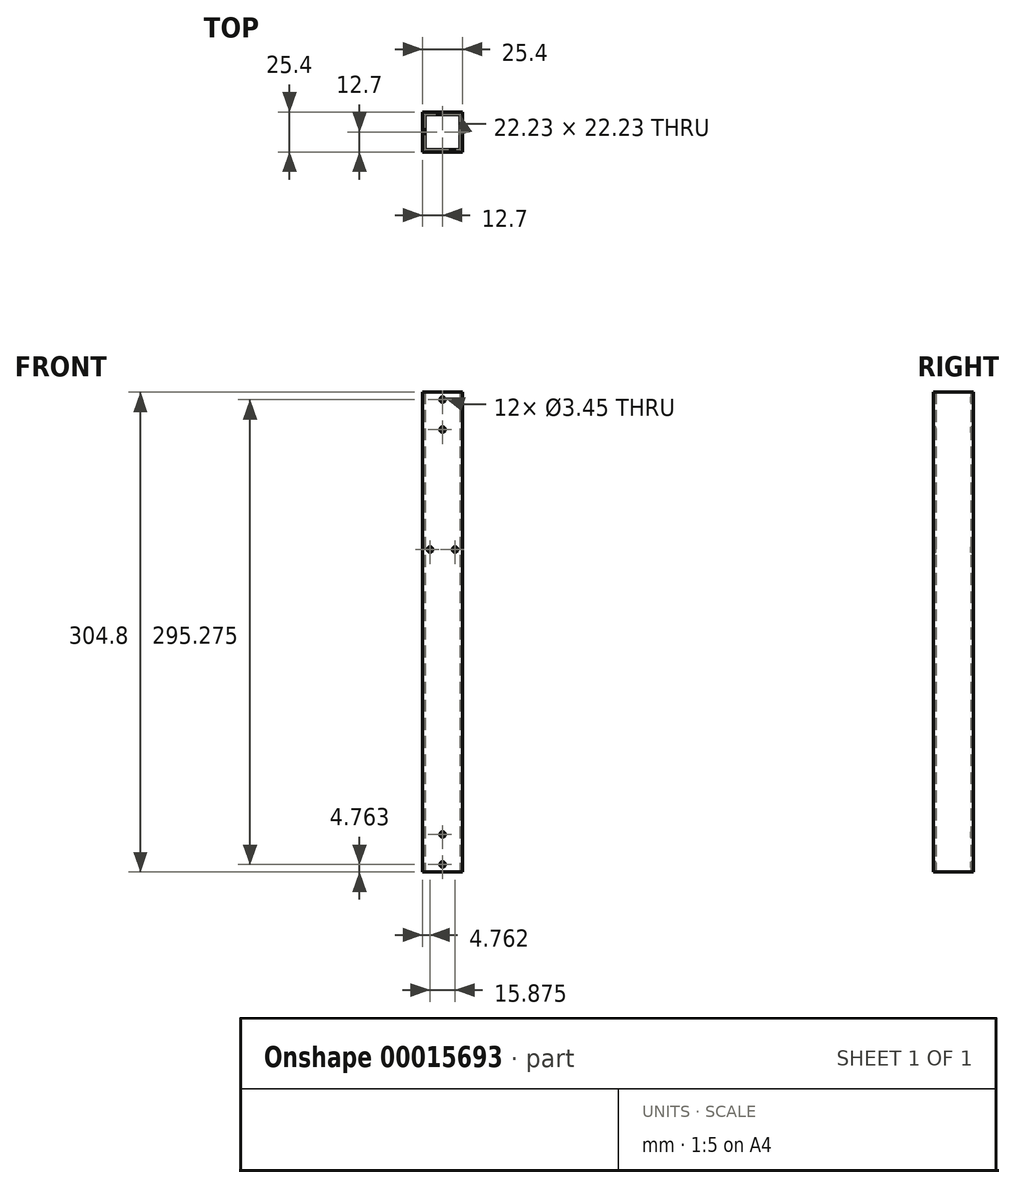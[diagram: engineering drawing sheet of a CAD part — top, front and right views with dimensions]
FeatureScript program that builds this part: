
annotation { "Feature Type Name" : "Feature", "Feature Type Description" : "" }
export const myFeature = defineFeature(function(context is Context, id is Id, definition is map)
    precondition{}
    {
        {
            var Q0;
            Q0=qCreatedBy(makeId("Top.planeOp"),FACE);
            var sketch = newSketch(context, id + "F0", { "sketchPlane" : qUnion([Q0])});
            skLineSegment(sketch, "E0.rect.bottom", {"start": v(12.7, -12.7) * mm, "end": v(-12.7, -12.7) * mm});
            skLineSegment(sketch, "E0.rect.top", {"start": v(12.7, 12.7) * mm, "end": v(-12.7, 12.7) * mm});
            skLineSegment(sketch, "E0.rect.left", {"start": v(12.7, -12.7) * mm, "end": v(12.7, 12.7) * mm});
            skLineSegment(sketch, "E0.rect.right", {"start": v(-12.7, -12.7) * mm, "end": v(-12.7, 12.7) * mm});
            skPoint(sketch, "E0.rect.middle", {"position": v(0, 0) * mm});
            skLineSegment(sketch, "E1.rect.bottom", {"start": v(11.11, -11.11) * mm, "end": v(-11.11, -11.11) * mm});
            skLineSegment(sketch, "E1.rect.top", {"start": v(11.11, 11.11) * mm, "end": v(-11.11, 11.11) * mm});
            skLineSegment(sketch, "E1.rect.left", {"start": v(11.11, -11.11) * mm, "end": v(11.11, 11.11) * mm});
            skLineSegment(sketch, "E1.rect.right", {"start": v(-11.11, -11.11) * mm, "end": v(-11.11, 11.11) * mm});
            skLineSegment(sketch, "E2", {"start": v(0, -11.11) * mm, "end": v(0, -12.7) * mm, "construction": true});
            skSolve(sketch);
        }
        {
            var Q0;
            Q0 = qSketchRegion(id + "F0", true);
            extrude(context, id + "F1", {"entities" : qUnion([Q0]), "depth" : 304.8 * mm});
        }
        {
            var Q0;
            Q0=makeQuery(id+"F1.opExtrude","SWEPT_FACE",FACE,{"disambiguationData":[OSD([sQuery(id+"F0.wireOp",EDGE,"E0.rect.bottom")])]});
            var sketch = newSketch(context, id + "F2", { "sketchPlane" : qUnion([Q0])});
            skLineSegment(sketch, "E3", {"start": v(0, 0) * mm, "end": v(0, 4.76) * mm, "construction": true});
            skLineSegment(sketch, "E4", {"start": v(0, 4.76) * mm, "end": v(0, 23.81) * mm, "construction": true});
            skCircle(sketch, "E5", {"center": v(0, 23.81) * mm, "radius": 1.73 * mm});
            skCircle(sketch, "E6", {"center": v(0, 4.76) * mm, "radius": 1.73 * mm});
            skLineSegment(sketch, "E7", {"start": v(0, 304.8) * mm, "end": v(0, 300.04) * mm, "construction": true});
            skLineSegment(sketch, "E8", {"start": v(0, 300.04) * mm, "end": v(0, 280.99) * mm, "construction": true});
            skCircle(sketch, "E9", {"center": v(0, 300.04) * mm, "radius": 1.73 * mm});
            skCircle(sketch, "E10", {"center": v(0, 280.99) * mm, "radius": 1.73 * mm});
            skLineSegment(sketch, "E11", {"start": v(12.7, 204.79) * mm, "end": v(7.94, 204.79) * mm, "construction": true});
            skLineSegment(sketch, "E12", {"start": v(7.94, 204.79) * mm, "end": v(-7.94, 204.79) * mm, "construction": true});
            skCircle(sketch, "E13", {"center": v(7.94, 204.79) * mm, "radius": 1.73 * mm});
            skCircle(sketch, "E14", {"center": v(-7.94, 204.79) * mm, "radius": 1.73 * mm});
            skLineSegment(sketch, "E15", {"start": v(0, 280.99) * mm, "end": v(0, 204.79) * mm, "construction": true});
            skSolve(sketch);
        }
        {
            var Q0;
            Q0 = qSketchRegion(id + "F2", true);
            var Q1;
            Q1=makeQuery(id+"F1.opExtrude","SWEPT_FACE",FACE,{"disambiguationData":[OSD([sQuery(id+"F0.wireOp",EDGE,"E0.rect.top")])]});
            extrude(context, id + "F3", {"entities" : qUnion([Q0]), "operationType" : NewBodyOperationType.REMOVE, "endBound" : BoundingType.UP_TO_SURFACE, "oppositeDirection" : true, "endBoundEntityFace" : qUnion([Q1]), "depth" : 25.4 * mm});
        }
    });
